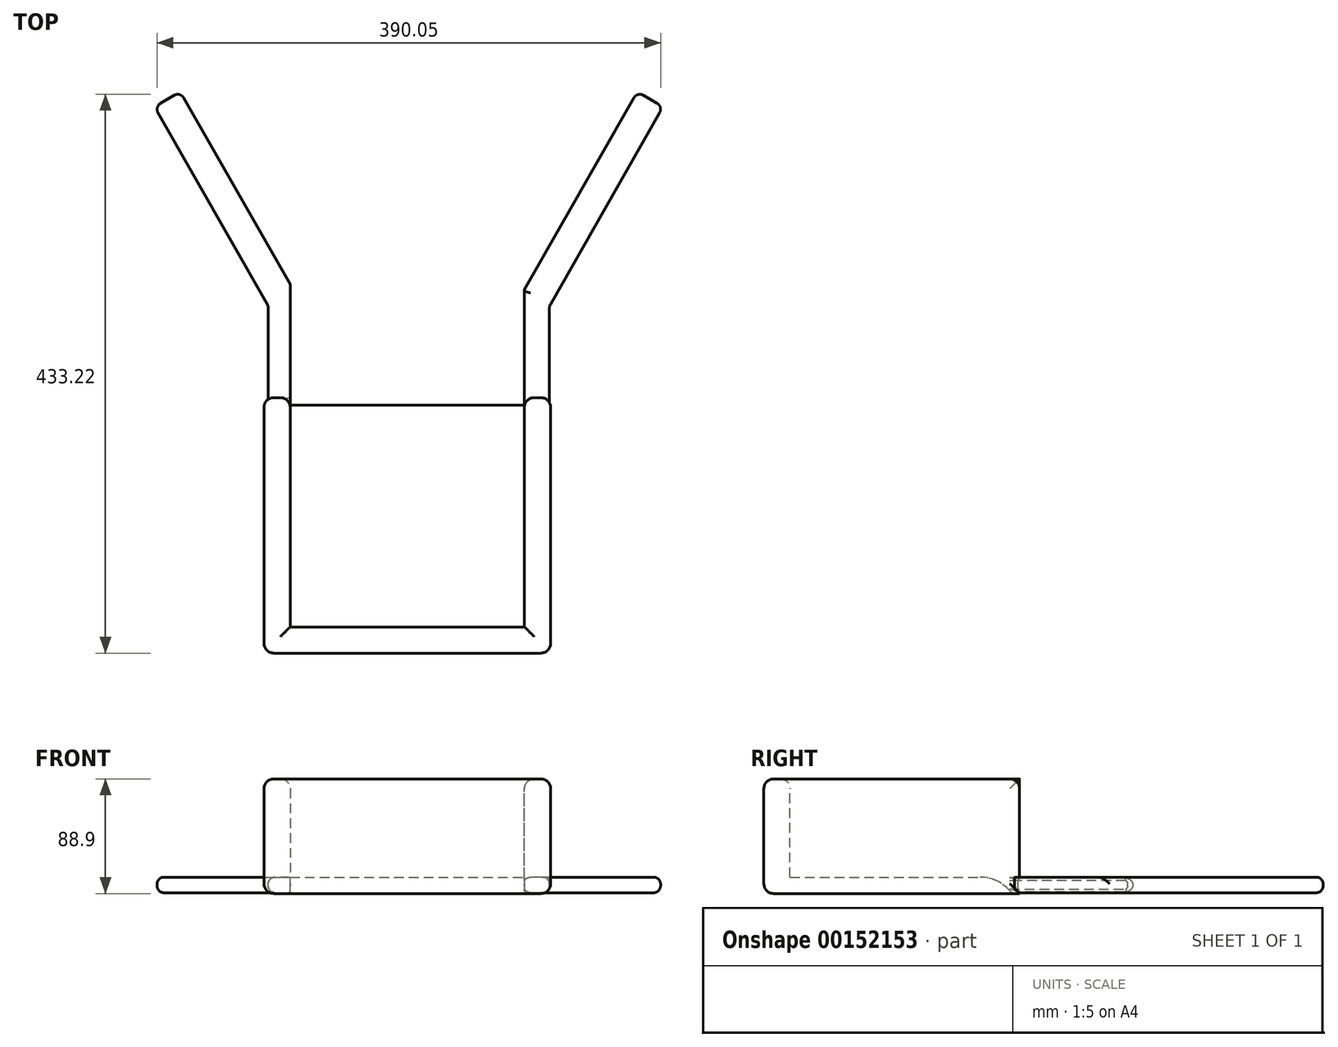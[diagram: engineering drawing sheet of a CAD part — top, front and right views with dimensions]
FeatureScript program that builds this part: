
annotation { "Feature Type Name" : "Feature", "Feature Type Description" : "" }
export const myFeature = defineFeature(function(context is Context, id is Id, definition is map)
    precondition{}
    {
        {
            var Q0;
            Q0=qCreatedBy(makeId("Front.planeOp"),FACE);
            var sketch = newSketch(context, id + "F0", { "sketchPlane" : qUnion([Q0])});
            skLineSegment(sketch, "E0.bottom", {"start": v(-112.02, 76.2) * mm, "end": v(-91.7, 76.2) * mm});
            skLineSegment(sketch, "E0.top", {"start": v(-112.02, 0) * mm, "end": v(-91.7, 0) * mm});
            skLineSegment(sketch, "E0.left", {"start": v(-112.02, 76.2) * mm, "end": v(-112.02, 0) * mm});
            skLineSegment(sketch, "E0.right", {"start": v(-91.7, 76.2) * mm, "end": v(-91.7, 0) * mm});
            skLineSegment(sketch, "E1.bottom", {"start": v(89.79, 0) * mm, "end": v(110.1, 0) * mm});
            skLineSegment(sketch, "E1.top", {"start": v(89.79, 76.2) * mm, "end": v(110.1, 76.2) * mm});
            skLineSegment(sketch, "E1.left", {"start": v(89.79, 0) * mm, "end": v(89.79, 76.2) * mm});
            skLineSegment(sketch, "E1.right", {"start": v(110.1, 0) * mm, "end": v(110.1, 76.2) * mm});
            skLineSegment(sketch, "E2.bottom", {"start": v(-112.02, 0) * mm, "end": v(110.1, 0) * mm});
            skLineSegment(sketch, "E2.top", {"start": v(-112.02, -12.7) * mm, "end": v(110.1, -12.7) * mm});
            skLineSegment(sketch, "E2.left", {"start": v(-112.02, 0) * mm, "end": v(-112.02, -12.7) * mm});
            skLineSegment(sketch, "E2.right", {"start": v(110.1, 0) * mm, "end": v(110.1, -12.7) * mm});
            skSolve(sketch);
        }
        {
            var Q0;
            Q0 = qSketchRegion(id + "F0", true);
            extrude(context, id + "F1", {"entities" : qUnion([Q0]), "depth" : 177.8 * mm});
        }
        {
            var Q0;
            Q0=makeQuery(id+"F1.opExtrude","CAP_FACE",FACE,{"disambiguationData":[OSD([sQuery(id+"F0.wireOp",EDGE,"E0.bottom"),sQuery(id+"F0.wireOp",EDGE,"E0.left"),sQuery(id+"F0.wireOp",EDGE,"E0.right"),sQuery(id+"F0.wireOp",EDGE,"E1.top"),sQuery(id+"F0.wireOp",EDGE,"E1.left"),sQuery(id+"F0.wireOp",EDGE,"E1.right"),sQuery(id+"F0.wireOp",EDGE,"E2.bottom"),sQuery(id+"F0.wireOp",EDGE,"E2.top"),sQuery(id+"F0.wireOp",EDGE,"E2.left"),sQuery(id+"F0.wireOp",EDGE,"E2.right")])],"isStart":false});
            var sketch = newSketch(context, id + "F2", { "sketchPlane" : qUnion([Q0])});
            skLineSegment(sketch, "E3.bottom", {"start": v(-112.02, 76.2) * mm, "end": v(110.1, 76.2) * mm});
            skLineSegment(sketch, "E3.top", {"start": v(-112.02, -12.7) * mm, "end": v(110.1, -12.7) * mm});
            skLineSegment(sketch, "E3.left", {"start": v(-112.02, 76.2) * mm, "end": v(-112.02, -12.7) * mm});
            skLineSegment(sketch, "E3.right", {"start": v(110.1, 76.2) * mm, "end": v(110.1, -12.7) * mm});
            skSolve(sketch);
        }
        {
            var Q0;
            Q0 = qSketchRegion(id + "F2", true);
            extrude(context, id + "F3", {"entities" : qUnion([Q0]), "operationType" : NewBodyOperationType.ADD, "depth" : 20.32 * mm});
        }
        {
            var Q0;
            Q0=qCreatedBy(makeId("Top.planeOp"),FACE);
            var sketch = newSketch(context, id + "F4", { "sketchPlane" : qUnion([Q0])});
            skLineSegment(sketch, "E4", {"start": v(-108.73, 0) * mm, "end": v(-88.66, 0) * mm});
            skLineSegment(sketch, "E5", {"start": v(-88.66, 0) * mm, "end": v(-88.66, 82.55) * mm});
            skLineSegment(sketch, "E6", {"start": v(-108.73, 0) * mm, "end": v(-108.73, 71.12) * mm});
            skLineSegment(sketch, "E7", {"start": v(-108.73, 71.12) * mm, "end": v(-88.66, 82.55) * mm});
            skLineSegment(sketch, "E8", {"start": v(109.2, 0) * mm, "end": v(89.14, 0) * mm});
            skLineSegment(sketch, "E9", {"start": v(89.14, 0) * mm, "end": v(89.14, 82.55) * mm});
            skLineSegment(sketch, "E10", {"start": v(109.2, 0) * mm, "end": v(109.2, 71.12) * mm});
            skLineSegment(sketch, "E11", {"start": v(109.2, 71.12) * mm, "end": v(89.14, 82.55) * mm});
            skSolve(sketch);
        }
        {
            var Q0;
            Q0 = qSketchRegion(id + "F4", true);
            extrude(context, id + "F5", {"entities" : qUnion([Q0]), "operationType" : NewBodyOperationType.ADD, "oppositeDirection" : true, "depth" : 12.06 * mm});
        }
        {
            var Q0;
            Q0=makeQuery(id+"F5.opExtrude","SWEPT_FACE",FACE,{"disambiguationData":[OSD([sQuery(id+"F4.wireOp",EDGE,"E7")])]});
            var sketch = newSketch(context, id + "F6", { "sketchPlane" : qUnion([Q0])});
            skLineSegment(sketch, "E12.bottom", {"start": v(36.18, 0) * mm, "end": v(59.28, 0) * mm});
            skLineSegment(sketch, "E12.top", {"start": v(36.18, -12.06) * mm, "end": v(59.28, -12.06) * mm});
            skLineSegment(sketch, "E12.left", {"start": v(36.18, 0) * mm, "end": v(36.18, -12.06) * mm});
            skLineSegment(sketch, "E12.right", {"start": v(59.28, 0) * mm, "end": v(59.28, -12.06) * mm});
            skSolve(sketch);
        }
        {
            var Q0;
            Q0=makeQuery(id+"F5.opExtrude","SWEPT_FACE",FACE,{"disambiguationData":[OSD([sQuery(id+"F4.wireOp",EDGE,"E11")])]});
            var sketch = newSketch(context, id + "F7", { "sketchPlane" : qUnion([Q0])});
            skLineSegment(sketch, "E13.bottom", {"start": v(-59.69, 0) * mm, "end": v(-36.6, 0) * mm});
            skLineSegment(sketch, "E13.top", {"start": v(-59.69, -12.06) * mm, "end": v(-36.6, -12.06) * mm});
            skLineSegment(sketch, "E13.left", {"start": v(-59.69, 0) * mm, "end": v(-59.69, -12.06) * mm});
            skLineSegment(sketch, "E13.right", {"start": v(-36.6, 0) * mm, "end": v(-36.6, -12.06) * mm});
            skSolve(sketch);
        }
        {
            var Q0;
            Q0=makeQuery(id+"F7.imprint","IMPRINT",FACE,{"disambiguationData":[TD([[makeQuery(id+"F7.imprint","IMPRINT",EDGE,{"derivedFrom":sQuery(id+"F7.wireOp",EDGE,"E13.bottom")}),-1.0]])]});
            extrude(context, id + "F8", {"entities" : qUnion([Q0]), "operationType" : NewBodyOperationType.ADD, "depth" : 177.8 * mm});
        }
        {
            var Q0;
            Q0=makeQuery(id+"F6.imprint","IMPRINT",FACE,{"disambiguationData":[TD([[makeQuery(id+"F6.imprint","IMPRINT",EDGE,{"derivedFrom":sQuery(id+"F6.wireOp",EDGE,"E12.bottom")}),1.0]])]});
            extrude(context, id + "F9", {"entities" : qUnion([Q0]), "operationType" : NewBodyOperationType.ADD, "depth" : 177.8 * mm});
        }
        {
            var Q0;
            Q0=makeQuery(id+"F9.boolean.opBoolean","MERGE",EDGE,{"derivedFrom":[makeQuery(id+"F5.opExtrude","SWEPT_EDGE",EDGE,{"disambiguationData":[OSD([sQuery(id+"F4.wireOp",EDGE,"E5"),sQuery(id+"F4.wireOp",EDGE,"E7")])]}),makeQuery(id+"F9.opExtrude","CAP_EDGE",EDGE,{"disambiguationData":[OSD([sQuery(id+"F6.wireOp",EDGE,"E12.left")])],"isStart":true})]});
            var Q1;
            Q1=makeQuery(id+"F5.opExtrude","CAP_EDGE",EDGE,{"disambiguationData":[OSD([sQuery(id+"F4.wireOp",EDGE,"E5")])],"isStart":false});
            var Q2;
            Q2=makeQuery(id+"F5.opExtrude","CAP_EDGE",EDGE,{"disambiguationData":[OSD([sQuery(id+"F4.wireOp",EDGE,"E5")])],"isStart":true});
            var Q3;
            Q3=makeQuery(id+"F5.opExtrude","CAP_EDGE",EDGE,{"disambiguationData":[OSD([sQuery(id+"F4.wireOp",EDGE,"E6")])],"isStart":true});
            var Q4;
            Q4=makeQuery(id+"F9.opExtrude","SWEPT_EDGE",EDGE,{"disambiguationData":[OSD([sQuery(id+"F6.wireOp",EDGE,"E12.bottom"),sQuery(id+"F6.wireOp",EDGE,"E12.left")])]});
            var Q5;
            Q5=makeQuery(id+"F9.opExtrude","SWEPT_EDGE",EDGE,{"disambiguationData":[OSD([sQuery(id+"F6.wireOp",EDGE,"E12.top"),sQuery(id+"F6.wireOp",EDGE,"E12.left")])]});
            var Q6;
            Q6=makeQuery(id+"F9.opExtrude","CAP_EDGE",EDGE,{"disambiguationData":[OSD([sQuery(id+"F6.wireOp",EDGE,"E12.bottom")])],"isStart":false});
            var Q7;
            Q7=makeQuery(id+"F9.opExtrude","CAP_EDGE",EDGE,{"disambiguationData":[OSD([sQuery(id+"F6.wireOp",EDGE,"E12.top")])],"isStart":false});
            var Q8;
            Q8=makeQuery(id+"F9.opExtrude","CAP_EDGE",EDGE,{"disambiguationData":[OSD([sQuery(id+"F6.wireOp",EDGE,"E12.left")])],"isStart":false});
            var Q9;
            Q9=makeQuery(id+"F5.opExtrude","CAP_EDGE",EDGE,{"disambiguationData":[OSD([sQuery(id+"F4.wireOp",EDGE,"E6")])],"isStart":false});
            var Q10;
            Q10=makeQuery(id+"F9.boolean.opBoolean","MERGE",EDGE,{"derivedFrom":[makeQuery(id+"F5.opExtrude","SWEPT_EDGE",EDGE,{"disambiguationData":[OSD([sQuery(id+"F4.wireOp",EDGE,"E6"),sQuery(id+"F4.wireOp",EDGE,"E7")])]}),makeQuery(id+"F9.opExtrude","CAP_EDGE",EDGE,{"disambiguationData":[OSD([sQuery(id+"F6.wireOp",EDGE,"E12.right")])],"isStart":true})]});
            var Q11;
            Q11=makeQuery(id+"F9.opExtrude","SWEPT_EDGE",EDGE,{"disambiguationData":[OSD([sQuery(id+"F6.wireOp",EDGE,"E12.top"),sQuery(id+"F6.wireOp",EDGE,"E12.right")])]});
            var Q12;
            Q12=makeQuery(id+"F9.opExtrude","SWEPT_EDGE",EDGE,{"disambiguationData":[OSD([sQuery(id+"F6.wireOp",EDGE,"E12.bottom"),sQuery(id+"F6.wireOp",EDGE,"E12.right")])]});
            var Q13;
            Q13=makeQuery(id+"F9.opExtrude","CAP_EDGE",EDGE,{"disambiguationData":[OSD([sQuery(id+"F6.wireOp",EDGE,"E12.right")])],"isStart":false});
            fillet(context, id + "F10", {"entities" : qUnion([Q0, Q1, Q2, Q3, Q4, Q5, Q6, Q7, Q8, Q9, Q10, Q11, Q12, Q13]), "radius" : 5.33 * mm, "tangentPropagation" : true, "allowEdgeOverflow" : false});
        }
        {
            var Q0;
            Q0=makeQuery(id+"F8.opExtrude","CAP_EDGE",EDGE,{"disambiguationData":[OSD([sQuery(id+"F7.wireOp",EDGE,"E13.right")])],"isStart":false});
            var Q1;
            Q1=makeQuery(id+"F8.opExtrude","SWEPT_EDGE",EDGE,{"disambiguationData":[OSD([sQuery(id+"F7.wireOp",EDGE,"E13.bottom"),sQuery(id+"F7.wireOp",EDGE,"E13.right")])]});
            var Q2;
            Q2=makeQuery(id+"F8.opExtrude","SWEPT_EDGE",EDGE,{"disambiguationData":[OSD([sQuery(id+"F7.wireOp",EDGE,"E13.top"),sQuery(id+"F7.wireOp",EDGE,"E13.right")])]});
            var Q3;
            Q3=makeQuery(id+"F8.opExtrude","CAP_EDGE",EDGE,{"disambiguationData":[OSD([sQuery(id+"F7.wireOp",EDGE,"E13.top")])],"isStart":false});
            var Q4;
            Q4=makeQuery(id+"F8.opExtrude","CAP_EDGE",EDGE,{"disambiguationData":[OSD([sQuery(id+"F7.wireOp",EDGE,"E13.bottom")])],"isStart":false});
            var Q5;
            Q5=makeQuery(id+"F8.opExtrude","CAP_EDGE",EDGE,{"disambiguationData":[OSD([sQuery(id+"F7.wireOp",EDGE,"E13.left")])],"isStart":false});
            var Q6;
            Q6=makeQuery(id+"F8.boolean.opBoolean","MERGE",EDGE,{"derivedFrom":[makeQuery(id+"F5.opExtrude","SWEPT_EDGE",EDGE,{"disambiguationData":[OSD([sQuery(id+"F4.wireOp",EDGE,"E10"),sQuery(id+"F4.wireOp",EDGE,"E11")])]}),makeQuery(id+"F8.opExtrude","CAP_EDGE",EDGE,{"disambiguationData":[OSD([sQuery(id+"F7.wireOp",EDGE,"E13.left")])],"isStart":true})]});
            var Q7;
            Q7=makeQuery(id+"F8.opExtrude","SWEPT_EDGE",EDGE,{"disambiguationData":[OSD([sQuery(id+"F7.wireOp",EDGE,"E13.bottom"),sQuery(id+"F7.wireOp",EDGE,"E13.left")])]});
            var Q8;
            Q8=makeQuery(id+"F8.opExtrude","SWEPT_EDGE",EDGE,{"disambiguationData":[OSD([sQuery(id+"F7.wireOp",EDGE,"E13.top"),sQuery(id+"F7.wireOp",EDGE,"E13.left")])]});
            var Q9;
            Q9=makeQuery(id+"F5.opExtrude","CAP_EDGE",EDGE,{"disambiguationData":[OSD([sQuery(id+"F4.wireOp",EDGE,"E10")])],"isStart":false});
            var Q10;
            Q10=makeQuery(id+"F5.opExtrude","CAP_EDGE",EDGE,{"disambiguationData":[OSD([sQuery(id+"F4.wireOp",EDGE,"E9")])],"isStart":false});
            var Q11;
            Q11=makeQuery(id+"F5.opExtrude","CAP_EDGE",EDGE,{"disambiguationData":[OSD([sQuery(id+"F4.wireOp",EDGE,"E9")])],"isStart":true});
            fillet(context, id + "F11", {"entities" : qUnion([Q0, Q1, Q2, Q3, Q4, Q5, Q6, Q7, Q8, Q9, Q10, Q11]), "radius" : 5.33 * mm, "tangentPropagation" : true, "allowEdgeOverflow" : false});
        }
        {
            var Q0;
            Q0=makeQuery(id+"F1.opExtrude","CAP_EDGE",EDGE,{"disambiguationData":[OSD([sQuery(id+"F0.wireOp",EDGE,"E2.bottom")])],"isStart":true});
            fillet(context, id + "F12", {"entities" : qUnion([Q0]), "radius" : 30.66 * mm, "tangentPropagation" : true, "allowEdgeOverflow" : false});
        }
        {
            var Q0;
            Q0=makeQuery(id+"F1.opExtrude","CAP_EDGE",EDGE,{"disambiguationData":[OSD([sQuery(id+"F0.wireOp",EDGE,"E1.right"),sQuery(id+"F0.wireOp",EDGE,"E2.right")])],"isStart":true});
            var Q1;
            Q1=makeQuery(id+"F1.opExtrude","CAP_EDGE",EDGE,{"disambiguationData":[OSD([sQuery(id+"F0.wireOp",EDGE,"E1.left")])],"isStart":true});
            var Q2;
            Q2=makeQuery(id+"F12.opFillet","TWEAK_EDGE",EDGE,{"disambiguationData":[OD(6.0)],"derivedFrom":[makeQuery(id+"F11.opFillet","MERGE",VERTEX,{"derivedFrom":[makeQuery(id+"F1.opExtrude","CAP_VERTEX",VERTEX,{"disambiguationData":[OSD([sQuery(id+"F0.wireOp",EDGE,"E1.left"),sQuery(id+"F0.wireOp",EDGE,"E2.bottom")])],"isStart":true}),makeQuery(id+"F5.opExtrude","CAP_VERTEX",VERTEX,{"disambiguationData":[OSD([sQuery(id+"F4.wireOp",EDGE,"E8"),sQuery(id+"F4.wireOp",EDGE,"E9")])],"isStart":true})]})]});
            var Q3;
            Q3=makeQuery(id+"F1.opExtrude","CAP_EDGE",EDGE,{"disambiguationData":[OSD([sQuery(id+"F0.wireOp",EDGE,"E1.top")])],"isStart":true});
            var Q4;
            Q4=makeQuery(id+"F3.boolean.opBoolean","MERGE",EDGE,{"derivedFrom":[makeQuery(id+"F1.opExtrude","SWEPT_EDGE",EDGE,{"disambiguationData":[OSD([sQuery(id+"F0.wireOp",EDGE,"E2.top"),sQuery(id+"F0.wireOp",EDGE,"E2.right")])]}),makeQuery(id+"F3.opExtrude","SWEPT_EDGE",EDGE,{"disambiguationData":[OSD([sQuery(id+"F2.wireOp",EDGE,"E3.top"),sQuery(id+"F2.wireOp",EDGE,"E3.right")])]})]});
            var Q5;
            Q5=makeQuery(id+"F3.boolean.opBoolean","MERGE",EDGE,{"derivedFrom":[makeQuery(id+"F1.opExtrude","SWEPT_EDGE",EDGE,{"disambiguationData":[OSD([sQuery(id+"F0.wireOp",EDGE,"E1.top"),sQuery(id+"F0.wireOp",EDGE,"E1.right")])]}),makeQuery(id+"F3.opExtrude","SWEPT_EDGE",EDGE,{"disambiguationData":[OSD([sQuery(id+"F2.wireOp",EDGE,"E3.bottom"),sQuery(id+"F2.wireOp",EDGE,"E3.right")])]})]});
            var Q6;
            Q6=makeQuery(id+"F3.opExtrude","CAP_EDGE",EDGE,{"disambiguationData":[OSD([sQuery(id+"F2.wireOp",EDGE,"E3.right")])],"isStart":false});
            var Q7;
            Q7=makeQuery(id+"F3.opExtrude","CAP_EDGE",EDGE,{"disambiguationData":[OSD([sQuery(id+"F2.wireOp",EDGE,"E3.top")])],"isStart":false});
            var Q8;
            Q8=makeQuery(id+"F3.opExtrude","CAP_EDGE",EDGE,{"disambiguationData":[OSD([sQuery(id+"F2.wireOp",EDGE,"E3.left")])],"isStart":false});
            var Q9;
            Q9=makeQuery(id+"F3.opExtrude","CAP_EDGE",EDGE,{"disambiguationData":[OSD([sQuery(id+"F2.wireOp",EDGE,"E3.bottom")])],"isStart":false});
            var Q10;
            Q10=makeQuery(id+"F3.boolean.opBoolean","MERGE",EDGE,{"derivedFrom":[makeQuery(id+"F1.opExtrude","SWEPT_EDGE",EDGE,{"disambiguationData":[OSD([sQuery(id+"F0.wireOp",EDGE,"E2.top"),sQuery(id+"F0.wireOp",EDGE,"E2.left")])]}),makeQuery(id+"F3.opExtrude","SWEPT_EDGE",EDGE,{"disambiguationData":[OSD([sQuery(id+"F2.wireOp",EDGE,"E3.top"),sQuery(id+"F2.wireOp",EDGE,"E3.left")])]})]});
            var Q11;
            Q11=makeQuery(id+"F3.boolean.opBoolean","MERGE",EDGE,{"derivedFrom":[makeQuery(id+"F1.opExtrude","SWEPT_EDGE",EDGE,{"disambiguationData":[OSD([sQuery(id+"F0.wireOp",EDGE,"E0.bottom"),sQuery(id+"F0.wireOp",EDGE,"E0.left")])]}),makeQuery(id+"F3.opExtrude","SWEPT_EDGE",EDGE,{"disambiguationData":[OSD([sQuery(id+"F2.wireOp",EDGE,"E3.bottom"),sQuery(id+"F2.wireOp",EDGE,"E3.left")])]})]});
            var Q12;
            Q12=makeQuery(id+"F1.opExtrude","SWEPT_EDGE",EDGE,{"disambiguationData":[OSD([sQuery(id+"F0.wireOp",EDGE,"E0.bottom"),sQuery(id+"F0.wireOp",EDGE,"E0.right")])]});
            var Q13;
            Q13=makeQuery(id+"F3.opExtrude","CAP_EDGE",EDGE,{"disambiguationData":[OSD([sQuery(id+"F2.wireOp",EDGE,"E3.bottom")])],"isStart":true});
            var Q14;
            Q14=makeQuery(id+"F1.opExtrude","SWEPT_EDGE",EDGE,{"disambiguationData":[OSD([sQuery(id+"F0.wireOp",EDGE,"E1.top"),sQuery(id+"F0.wireOp",EDGE,"E1.left")])]});
            var Q15;
            Q15=makeQuery(id+"F1.opExtrude","CAP_EDGE",EDGE,{"disambiguationData":[OSD([sQuery(id+"F0.wireOp",EDGE,"E0.right")])],"isStart":true});
            var Q16;
            Q16=makeQuery(id+"F1.opExtrude","CAP_EDGE",EDGE,{"disambiguationData":[OSD([sQuery(id+"F0.wireOp",EDGE,"E0.left"),sQuery(id+"F0.wireOp",EDGE,"E2.left")])],"isStart":true});
            fillet(context, id + "F13", {"entities" : qUnion([Q0, Q1, Q2, Q3, Q4, Q5, Q6, Q7, Q8, Q9, Q10, Q11, Q12, Q13, Q14, Q15, Q16]), "radius" : 7.62 * mm, "tangentPropagation" : true, "allowEdgeOverflow" : false});
        }
    });
